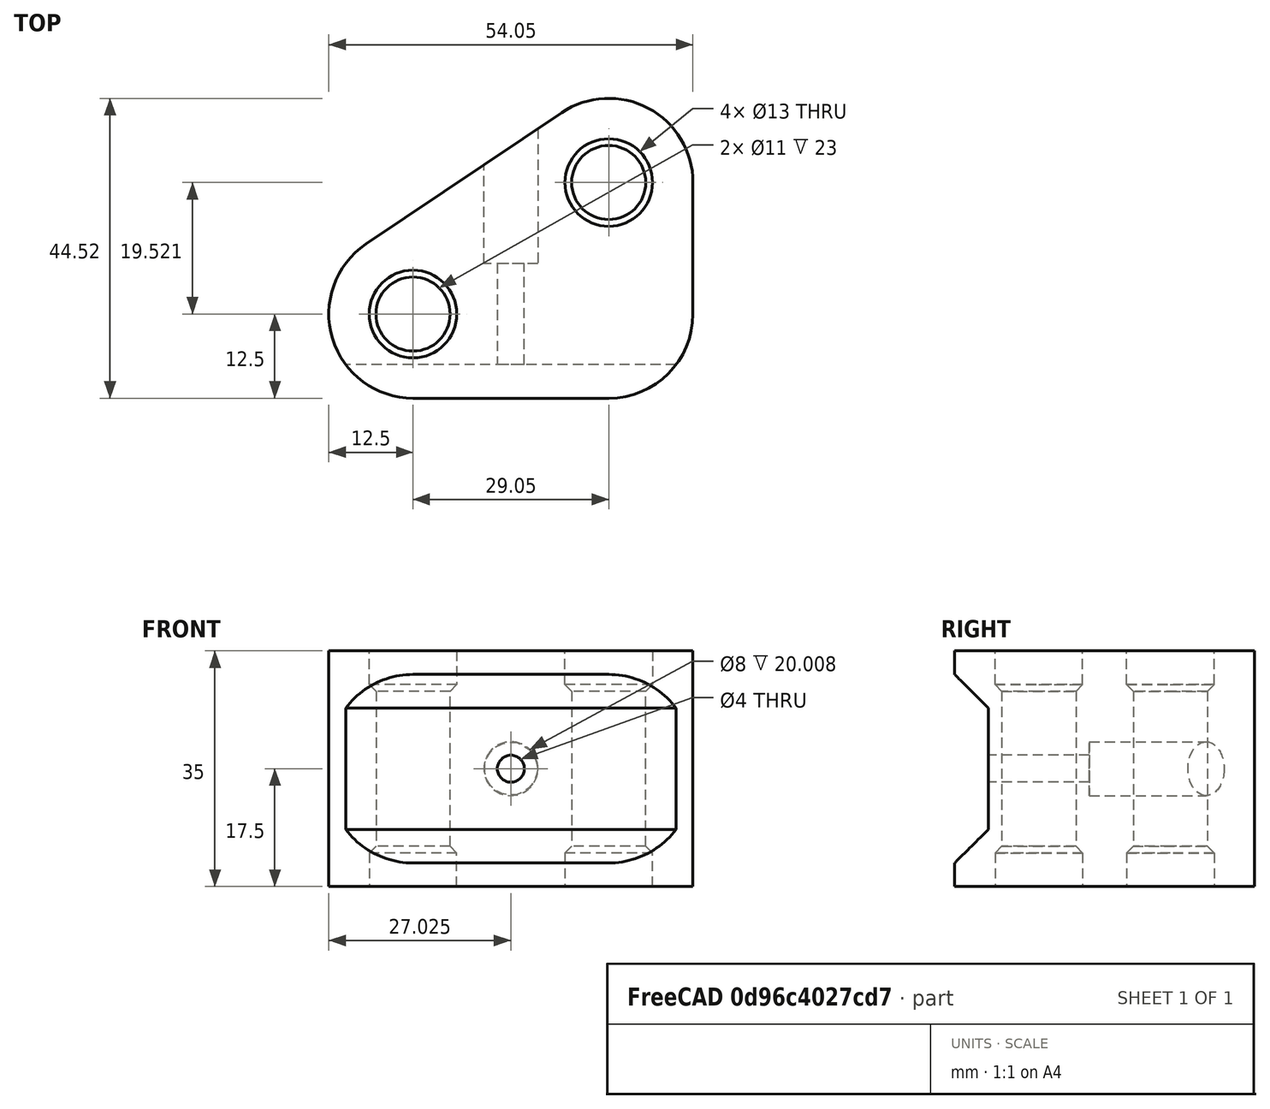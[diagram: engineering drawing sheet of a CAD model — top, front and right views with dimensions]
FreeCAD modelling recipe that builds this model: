
FCSTD DOCUMENT  (FreeCAD 0.20R29177 +426 (Git))
Label: #21_EndEffector
License: All rights reserved
LicenseURL: http://en.wikipedia.org/wiki/All_rights_reserved
objects: Sketcher::SketchObject×6, PartDesign::Pocket×5, TechDraw::DrawProjGroupItem×5, TechDraw::DrawViewDimension×5, PartDesign::Pad×1, PartDesign::Chamfer×1, PartDesign::Plane×1, PartDesign::Body×1, Part::FeaturePython×1, TechDraw::DrawSVGTemplate×1, TechDraw::DrawProjGroup×1, TechDraw::DrawPage×1
note: 23 computed .brp shape members not serialized (recipe doc carries the construction recipe); baked Part::Feature solids carry a one-line shape summary decoded from their .brp

FEATURE [Sketcher::SketchObject] Sketch
  FullyConstrained = true
  MapMode = 5
  Support = -> [XY_Plane]
  sketch-geometry (11):
    g0: Circle CenterX=0 CenterY=0 CenterZ=0 NormalX=0 NormalY=0 NormalZ=1 AngleXU=0 Radius=5.5
    g1: Circle CenterX=29.0504 CenterY=19.5211 CenterZ=0 NormalX=0 NormalY=0 NormalZ=1 AngleXU=0 Radius=5.5
    g2: LineSegment StartX=0 StartY=0 StartZ=0 EndX=29.0504 EndY=19.5211 EndZ=0
    g3: GeomPoint X=29.0504 Y=0 Z=0
    g4: LineSegment StartX=29.0504 StartY=0 StartZ=0 EndX=29.0504 EndY=19.5211 EndZ=0
    g5: ArcOfCircle CenterX=29.0504 CenterY=0 CenterZ=0 NormalX=0 NormalY=0 NormalZ=1 AngleXU=0 Radius=12.5 StartAngle=4.71239 EndAngle=6.28319
    g6: ArcOfCircle CenterX=29.0504 CenterY=19.5211 CenterZ=0 NormalX=0 NormalY=0 NormalZ=1 AngleXU=0 Radius=12.5 StartAngle=0 EndAngle=2.16246
    g7: ArcOfCircle CenterX=0 CenterY=0 CenterZ=0 NormalX=0 NormalY=0 NormalZ=1 AngleXU=0 Radius=12.5 StartAngle=2.16246 EndAngle=4.71239
    g8: LineSegment StartX=-6.97181 StartY=10.3752 StartZ=0 EndX=22.0786 EndY=29.8962 EndZ=0
    g9: LineSegment StartX=41.5504 StartY=19.5211 StartZ=0 EndX=41.5504 EndY=0 EndZ=0
    g10: LineSegment StartX=29.0504 StartY=-12.5 StartZ=0 EndX=0 EndY=-12.5 EndZ=0
  constraints (23):
    c: Coincident(g0,g-1)
    c: Coincident(g2,g0)
    c: Coincident(g2,g1)
    c: Distance(g2) = 35
    c: Diameter(g1) = 11
    c: Equal(g1,g0)
    c: Angle(g-1,g2) = 0.591667
    c: PointOnObject(g3,g-1)
    c: Coincident(g4,g3)
    c: Coincident(g4,g1)
    c: Vertical(g4)
    c: Coincident(g5,g3)
    c: Coincident(g6,g1)
    c: Coincident(g7,g0)
    c: Diameter(g6) = 25
    c: Diameter(g5) = 25
    c: Diameter(g7) = 25
    c: Tangent(g9,g6) = 1.5708
    c: Tangent(g9,g5) = 1.5708
    c: Tangent(g10,g5) = 1.5708
    c: Tangent(g10,g7) = 1.5708
    c: Tangent(g8,g7) = 1.5708
    c: Tangent(g8,g6) = 1.5708
FEATURE [PartDesign::Pad] Pad
  Direction = (0,0,1)
  Length = 35
  Length2 = 10
  Profile = -> Sketch
  ReferenceAxis = -> Sketch [N_Axis]
  Refine = true
  Type = 0
FEATURE [Sketcher::SketchObject] Sketch001
  ExternalGeometry = -> [Pad]
  FullyConstrained = true
  MapMode = 5
  Placement = pos=(0,0,35) rot=(0,0,1;0rad)
  Support = -> [Pad]
  sketch-geometry (2):
    g0: Circle CenterX=0 CenterY=0 CenterZ=0 NormalX=0 NormalY=0 NormalZ=1 AngleXU=0 Radius=6.5
    g1: Circle CenterX=29.0504 CenterY=19.5211 CenterZ=0 NormalX=0 NormalY=0 NormalZ=1 AngleXU=0 Radius=6.5
  constraints (4):
    c: Coincident(g0,g-1)
    c: Coincident(g1,g-3)
    c: Diameter(g0) = 13
    c: Diameter(g1) = 13
FEATURE [PartDesign::Pocket] Pocket
  BaseFeature = -> Pad
  Direction = (0,0,-1)
  Length = 6
  Length2 = 5
  Profile = -> Sketch001
  ReferenceAxis = -> Sketch001 [N_Axis]
  Refine = true
  Type = 0
FEATURE [Sketcher::SketchObject] Sketch002
  ExternalGeometry = -> [Pocket]
  FullyConstrained = true
  MapMode = 5
  Placement = pos=(0,0,0) rot=(1,0,0;3.14159rad)
  Support = -> [Pocket]
  sketch-geometry (2):
    g0: Circle CenterX=0 CenterY=0 CenterZ=0 NormalX=0 NormalY=0 NormalZ=1 AngleXU=0 Radius=6.5
    g1: Circle CenterX=29.0504 CenterY=-19.5211 CenterZ=0 NormalX=0 NormalY=0 NormalZ=1 AngleXU=0 Radius=6.5
  constraints (4):
    c: Coincident(g0,g-1)
    c: Coincident(g1,g-3)
    c: Diameter(g1) = 13
    c: Diameter(g0) = 13
FEATURE [PartDesign::Pocket] Pocket001
  BaseFeature = -> Pocket
  Direction = (0,0,1)
  Length = 6
  Length2 = 5
  Profile = -> Sketch002
  ReferenceAxis = -> Sketch002 [N_Axis]
  Refine = true
  Type = 0
FEATURE [PartDesign::Chamfer] Chamfer
  Angle = 45
  Base = -> Pocket001 [Edge24,Edge26,Edge30,Edge28]
  BaseFeature = -> Pocket001
  ChamferType = 0
  FlipDirection = false
  Refine = true
  Size = 0.99999
  Size2 = 1
  SupportTransform = false
  UseAllEdges = false
FEATURE [Sketcher::SketchObject] Sketch003
  ExternalGeometry = -> [Chamfer]
  FullyConstrained = true
  MapMode = 5
  Placement = pos=(0,-12.5,0) rot=(1,0,0;1.5708rad)
  Support = -> [Chamfer]
  sketch-geometry (1):
    g0: Circle CenterX=14.5252 CenterY=17.5 CenterZ=0 NormalX=0 NormalY=0 NormalZ=1 AngleXU=0 Radius=2
  constraints (2):
    c: Diameter(g0) = 4
    c: Symmetric(g-3,g-1,g0)
FEATURE [PartDesign::Pocket] Pocket002
  BaseFeature = -> Chamfer
  Direction = (0,1,-2e-16)
  Length = 40
  Length2 = 5
  Profile = -> Sketch003
  ReferenceAxis = -> Sketch003 [N_Axis]
  Refine = true
  Type = 0
FEATURE [PartDesign::Plane] DatumPlane
  AttachmentOffset = pos=(0,0,-60) rot=(0,0,1;0rad)
  Length = 60
  MapMode = 5
  Placement = pos=(0,47.5,-1.33e-14) rot=(1,0,0;1.5708rad)
  ResizeMode = 0
  Support = -> [Pocket002]
  Width = 60
FEATURE [Sketcher::SketchObject] Sketch004
  ExternalGeometry = -> [Pocket002]
  FullyConstrained = true
  MapMode = 5
  Placement = pos=(0,47.5,-1.33e-14) rot=(1,0,0;1.5708rad)
  Support = -> [DatumPlane]
  sketch-geometry (1):
    g0: Circle CenterX=14.5252 CenterY=17.5 CenterZ=0 NormalX=0 NormalY=0 NormalZ=1 AngleXU=0 Radius=4
  constraints (2):
    c: Coincident(g0,g-3)
    c: Diameter(g0) = 8
FEATURE [PartDesign::Pocket] Pocket003
  BaseFeature = -> Pocket002
  Direction = (0,1,-2e-16)
  Length = 40
  Length2 = 5
  Profile = -> Sketch004
  ReferenceAxis = -> Sketch004 [N_Axis]
  Refine = true
  Reversed = true
  Type = 0
FEATURE [Sketcher::SketchObject] Sketch005
  ExternalGeometry = -> [Pocket003]
  FullyConstrained = true
  MapMode = 5
  Placement = pos=(41.5504,0,0) rot=(0.57735,0.57735,0.57735;2.0944rad)
  Support = -> [Pocket003]
  sketch-geometry (6):
    g0: LineSegment StartX=-12.5 StartY=31.5 StartZ=0 EndX=-7.5 EndY=26.5 EndZ=0
    g1: LineSegment StartX=-7.5 StartY=26.5 StartZ=0 EndX=-7.5 EndY=8.5 EndZ=0
    g2: LineSegment StartX=-7.5 StartY=8.5 StartZ=0 EndX=-12.5 EndY=3.5 EndZ=0
    g3: LineSegment StartX=-12.5 StartY=31.5 StartZ=0 EndX=-12.5 EndY=3.5 EndZ=0
    g4: LineSegment StartX=-12.5 StartY=31.5 StartZ=0 EndX=-12.5 EndY=35 EndZ=0
    g5: LineSegment StartX=-12.5 StartY=3.5 StartZ=0 EndX=-12.5 EndY=0 EndZ=0
  constraints (16):
    c: PointOnObject(g0,g-3)
    c: Coincident(g1,g0)
    c: Vertical(g1)
    c: Coincident(g2,g1)
    c: PointOnObject(g2,g-3)
    c: Distance(g1) = 18
    c: Angle(g2,g-3) = 0.785398
    c: Angle(g-3,g0) = 0.785398
    c: Coincident(g3,g2)
    c: Coincident(g4,g0)
    c: Coincident(g4,g-4)
    c: Coincident(g5,g2)
    c: Coincident(g5,g-3)
    c: Equal(g5,g4)
    c: Distance(g5) = 3.5
    c: Coincident(g3,g0)
FEATURE [PartDesign::Pocket] Pocket004
  BaseFeature = -> Pocket003
  Direction = (-1,0,0)
  Length = 80
  Length2 = 5
  Profile = -> Sketch005
  ReferenceAxis = -> Sketch005 [N_Axis]
  Refine = true
  Type = 0
FEATURE [PartDesign::Body] Body
  Group = -> [Sketch,Pad,Sketch001,Pocket,Sketch002,Pocket001,Chamfer,Sketch003,Pocket002,DatumPlane,Sketch004,Pocket003,Sketch005,Pocket004]
  Origin = -> Origin
  Tip = -> Pocket004
FEATURE [Part::FeaturePython] refine  label="refine_Pocket004"  # WARN: FeaturePython — macro-defined, semantics opaque (R4)
  Base = -> Pocket004
FEATURE [TechDraw::DrawSVGTemplate] Template
  EditableTexts = Designed_by_Name=Designed by Name; Drawing_number=Drawing number; FC-Date=Date; FC-SC=Scale; FC-SH=Sheet; FC-Title=Title; Subtitle=Subtitle; Weight=Weight
  Height = 210
  Orientation = 1
  Width = 297
FEATURE [TechDraw::DrawProjGroupItem] ProjItem  label="Front"
  Caption = Front
  CoarseView = false
  Direction = (0,0,1)
  Focus = 100
  HardHidden = false
  IsoCount = 0
  IsoHidden = false
  IsoVisible = false
  LockPosition = true
  Perspective = false
  Rotation = 0
  RotationVector = (1,0,0)
  Scale = 0.75
  ScaleType = 2
  SeamHidden = false
  SeamVisible = true
  SmoothHidden = false
  SmoothVisible = true
  Source = -> [refine]
  Type = 0
  X = 0
  XDirection = (1,0,0)
  Y = 0
FEATURE [TechDraw::DrawProjGroupItem] ProjItem001  label="Right"
  Caption = Right
  CoarseView = false
  Direction = (1,0,1e-16)
  Focus = 100
  HardHidden = false
  IsoCount = 0
  IsoHidden = false
  IsoVisible = false
  LockPosition = false
  Perspective = false
  Rotation = 0
  RotationVector = (1,0,0)
  Scale = 0.75
  ScaleType = 2
  SeamHidden = false
  SeamVisible = true
  SmoothHidden = false
  SmoothVisible = true
  Source = -> [refine]
  Type = 2
  X = -53.5661
  XDirection = (1e-16,0,-1)
  Y = 0
FEATURE [TechDraw::DrawProjGroupItem] ProjItem002  label="Top"
  Caption = Top
  CoarseView = false
  Direction = (0,1,0)
  Focus = 100
  HardHidden = false
  IsoCount = 0
  IsoHidden = false
  IsoVisible = false
  LockPosition = false
  Perspective = false
  Rotation = 0
  RotationVector = (1,0,0)
  Scale = 0.75
  ScaleType = 2
  SeamHidden = false
  SeamVisible = true
  SmoothHidden = false
  SmoothVisible = true
  Source = -> [refine]
  Type = 4
  X = 0
  XDirection = (1,0,0)
  Y = -58.2728
FEATURE [TechDraw::DrawProjGroupItem] ProjItem003  label="FrontTopLeft"
  Caption = Perspective (internals)
  CoarseView = false
  Direction = (-0.57735,0.57735,0.57735)
  Focus = 100
  HardHidden = true
  IsoCount = 0
  IsoHidden = false
  IsoVisible = false
  LockPosition = false
  Perspective = false
  Rotation = 0
  RotationVector = (1,0,0)
  Scale = 0.75
  ScaleType = 2
  SeamHidden = false
  SeamVisible = true
  SmoothHidden = false
  SmoothVisible = true
  Source = -> [refine]
  Type = 6
  X = 83.4214
  XDirection = (0.707107,0,0.707107)
  Y = -64.6261
FEATURE [TechDraw::DrawProjGroupItem] ProjItem004  label="FrontBottomLeft"
  Caption = Perspective
  CoarseView = false
  Direction = (-0.57735,-0.57735,0.57735)
  Focus = 100
  HardHidden = false
  IsoCount = 0
  IsoHidden = false
  IsoVisible = false
  LockPosition = false
  Perspective = false
  Rotation = 0
  RotationVector = (1,0,0)
  Scale = 0.75
  ScaleType = 2
  SeamHidden = false
  SeamVisible = true
  SmoothHidden = false
  SmoothVisible = true
  Source = -> [refine]
  Type = 8
  X = 84.2964
  XDirection = (0.707107,0,0.707107)
  Y = -2.20885
FEATURE [TechDraw::DrawProjGroup] ProjGroup
  Anchor = -> ProjItem
  AutoDistribute = false
  LockPosition = false
  ProjectionType = 0
  Rotation = 0
  Scale = 0.75
  ScaleType = 2
  Source = -> [refine]
  Views = -> [ProjItem,ProjItem001,ProjItem002,ProjItem003,ProjItem004]
  X = 146.038
  Y = 166.384
  spacingX = 15
  spacingY = 15
FEATURE [TechDraw::DrawViewDimension] Dimension
  AngleOverride = false
  Arbitrary = false
  ArbitraryTolerances = false
  EqualTolerance = true
  ExtensionAngle = 0
  FormatSpec = %.2w
  FormatSpecOverTolerance = %+.2w
  FormatSpecUnderTolerance = %+.2w
  Inverted = false
  LineAngle = 0
  LockPosition = false
  MeasureType = 1
  OverTolerance = 0
  References2D = -> [ProjItem001]
  Rotation = 0
  ScaleType = 0
  TheoreticalExact = false
  Type = 1
  UnderTolerance = 0
  X = -0.153196
  Y = 3.21558
FEATURE [TechDraw::DrawViewDimension] Dimension001
  AngleOverride = false
  Arbitrary = false
  ArbitraryTolerances = false
  EqualTolerance = true
  ExtensionAngle = 0
  FormatSpec = %.2w
  FormatSpecOverTolerance = %+.2w
  FormatSpecUnderTolerance = %+.2w
  Inverted = false
  LineAngle = 0
  LockPosition = false
  MeasureType = 1
  OverTolerance = 0
  References2D = -> [ProjItem001]
  Rotation = 0
  ScaleType = 0
  TheoreticalExact = false
  Type = 6
  UnderTolerance = 0
  X = 18.153
  Y = -5.60171
FEATURE [TechDraw::DrawViewDimension] Dimension002
  AngleOverride = false
  Arbitrary = false
  ArbitraryTolerances = false
  EqualTolerance = true
  ExtensionAngle = 0
  FormatSpec = %.2w
  FormatSpecOverTolerance = %+.2w
  FormatSpecUnderTolerance = %+.2w
  Inverted = false
  LineAngle = 0
  LockPosition = false
  MeasureType = 1
  OverTolerance = 0
  References2D = -> [ProjItem001]
  Rotation = 0
  ScaleType = 0
  TheoreticalExact = false
  Type = 2
  UnderTolerance = 0
  X = -20.9316
  Y = -12.9931
FEATURE [TechDraw::DrawViewDimension] Dimension003
  AngleOverride = false
  Arbitrary = false
  ArbitraryTolerances = false
  EqualTolerance = true
  ExtensionAngle = 0
  FormatSpec = %.2w
  FormatSpecOverTolerance = %+.2w
  FormatSpecUnderTolerance = %+.2w
  Inverted = false
  LineAngle = 0
  LockPosition = false
  MeasureType = 1
  OverTolerance = 0
  References2D = -> [ProjItem001]
  Rotation = 0
  ScaleType = 0
  TheoreticalExact = false
  Type = 1
  UnderTolerance = 0
  X = -0.120995
  Y = 26.2397
FEATURE [TechDraw::DrawViewDimension] Dimension004
  AngleOverride = false
  Arbitrary = false
  ArbitraryTolerances = false
  EqualTolerance = true
  ExtensionAngle = 0
  FormatSpec = %.2w
  FormatSpecOverTolerance = %+.2w
  FormatSpecUnderTolerance = %+.2w
  Inverted = false
  LineAngle = 0
  LockPosition = false
  MeasureType = 1
  OverTolerance = 0
  References2D = -> [ProjItem]
  Rotation = 0
  ScaleType = 0
  TheoreticalExact = false
  Type = 1
  UnderTolerance = 0
  X = -0.092668
  Y = -8.73272
FEATURE [TechDraw::DrawPage] Page
  KeepUpdated = true
  NextBalloonIndex = 1
  ProjectionType = 0
  Template = -> Template
  Views = -> [ProjGroup,Dimension,Dimension001,Dimension002,Dimension003,Dimension004]
